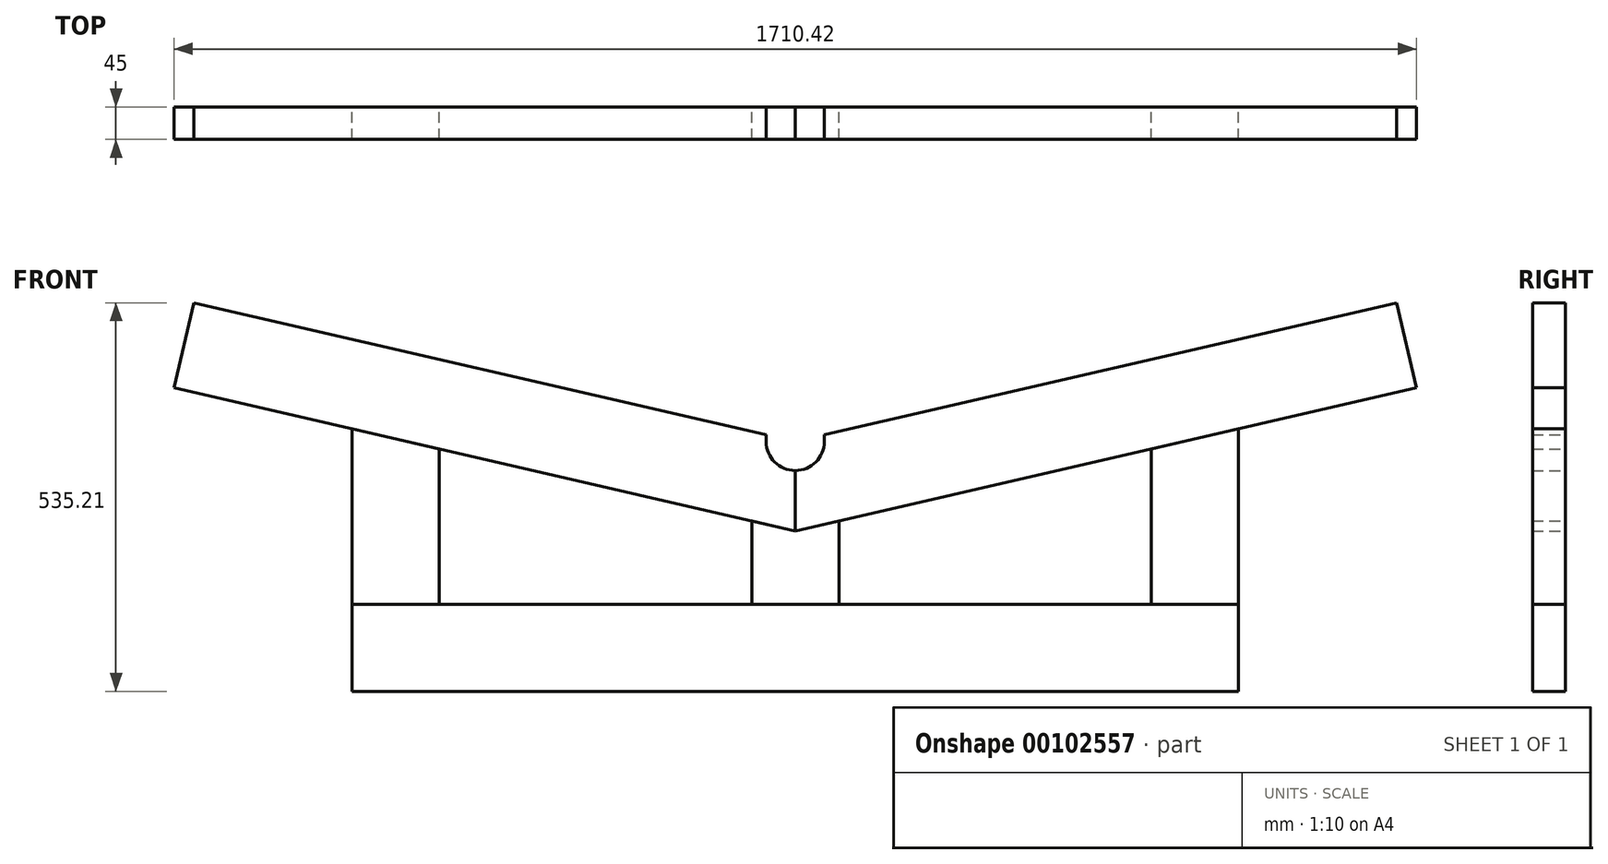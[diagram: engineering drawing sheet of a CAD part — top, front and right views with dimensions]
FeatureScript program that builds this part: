
annotation { "Feature Type Name" : "Feature", "Feature Type Description" : "" }
export const myFeature = defineFeature(function(context is Context, id is Id, definition is map)
    precondition{}
    {
        {
            var Q0;
            Q0=qCreatedBy(makeId("Front.planeOp"),FACE);
            var sketch = newSketch(context, id + "F0", { "sketchPlane" : qUnion([Q0])});
            skLineSegment(sketch, "E0.bottom", {"start": v(0, 0) * mm, "end": v(1220, 0) * mm});
            skLineSegment(sketch, "E0.top", {"start": v(0, 120) * mm, "end": v(1220, 120) * mm});
            skLineSegment(sketch, "E0.left", {"start": v(0, 0) * mm, "end": v(0, 120) * mm});
            skLineSegment(sketch, "E0.right", {"start": v(1220, 0) * mm, "end": v(1220, 120) * mm});
            skSolve(sketch);
        }
        {
            var Q0;
            Q0 = qSketchRegion(id + "F0", true);
            extrude(context, id + "F1", {"entities" : qUnion([Q0]), "depth" : 45 * mm});
        }
        {
            var Q0;
            Q0=qCreatedBy(makeId("Front.planeOp"),FACE);
            var sketch = newSketch(context, id + "F2", { "sketchPlane" : qUnion([Q0])});
            skLineSegment(sketch, "E1", {"start": v(610, 0) * mm, "end": v(610, 344) * mm, "construction": true});
            skLineSegment(sketch, "E2", {"start": v(570, 353.23) * mm, "end": v(-218.21, 535.2) * mm});
            skLineSegment(sketch, "E3.0", {"start": v(610, 220.84) * mm, "end": v(-245.2, 418.28) * mm});
            skLineSegment(sketch, "E4", {"start": v(-218.21, 535.2) * mm, "end": v(-245.2, 418.28) * mm});
            skLineSegment(sketch, "E5", {"start": v(610, 220.84) * mm, "end": v(610, 304) * mm});
            skArc(sketch, "E6", {"start": v(570, 344) * mm, "mid": v(581.72, 315.72) * mm, "end": v(610, 304) * mm});
            skLineSegment(sketch, "E7", {"start": v(570, 344) * mm, "end": v(570, 353.23) * mm});
            skSolve(sketch);
        }
        {
            var Q0;
            Q0 = qSketchRegion(id + "F2", true);
            extrude(context, id + "F3", {"entities" : qUnion([Q0]), "depth" : 45 * mm});
        }
        {
            var Q0;
            Q0=qCreatedBy(makeId("Front.planeOp"),FACE);
            var sketch = newSketch(context, id + "F4", { "sketchPlane" : qUnion([Q0])});
            skLineSegment(sketch, "E8", {"start": v(0, 120) * mm, "end": v(0, 361.67) * mm});
            skLineSegment(sketch, "E9.0", {"start": v(120, 120) * mm, "end": v(120, 333.97) * mm});
            skLineSegment(sketch, "E10", {"start": v(0, 361.67) * mm, "end": v(120, 333.97) * mm});
            skLineSegment(sketch, "E11", {"start": v(0, 120) * mm, "end": v(120, 120) * mm});
            skSolve(sketch);
        }
        {
            var Q0;
            Q0 = qSketchRegion(id + "F4", true);
            extrude(context, id + "F5", {"entities" : qUnion([Q0]), "depth" : 45 * mm});
        }
        {
            var Q0;
            Q0=qCreatedBy(makeId("Right.planeOp"),FACE);
            cPlane(context, id + "F6", {"entities" : qUnion([Q0]), "cplaneType" : CPlaneType.OFFSET, "offset" : 610 * mm, "width" : 150 * mm, "height" : 150 * mm});
        }
        {
            var Q0;
            Q0=makeQuery(id+"F1.opExtrude","SWEPT_BODY",BODY,{"disambiguationData":[OSD([sQuery(id+"F0.wireOp",EDGE,"E0.bottom"),sQuery(id+"F0.wireOp",EDGE,"E0.top"),sQuery(id+"F0.wireOp",EDGE,"E0.left"),sQuery(id+"F0.wireOp",EDGE,"E0.right")])]});
            var Q1;
            Q1=makeQuery(id+"F3.opExtrude","SWEPT_BODY",BODY,{"disambiguationData":[OSD([sQuery(id+"F2.wireOp",EDGE,"E2"),sQuery(id+"F2.wireOp",EDGE,"E3.0"),sQuery(id+"F2.wireOp",EDGE,"E4"),sQuery(id+"F2.wireOp",EDGE,"E5"),sQuery(id+"F2.wireOp",EDGE,"E6"),sQuery(id+"F2.wireOp",EDGE,"E7")])]});
            var Q2;
            Q2=makeQuery(id+"F5.opExtrude","SWEPT_BODY",BODY,{"disambiguationData":[OSD([sQuery(id+"F4.wireOp",EDGE,"E8"),sQuery(id+"F4.wireOp",EDGE,"E9.0"),sQuery(id+"F4.wireOp",EDGE,"E10"),sQuery(id+"F4.wireOp",EDGE,"E11")])]});
            var Q3;
            Q3=qCreatedBy(id+"F6.planeOp",FACE);
            mirror(context, id + "F7", {"entities" : qUnion([Q0, Q1, Q2]), "mirrorPlane" : qUnion([Q3])});
        }
        {
            var Q0;
            Q0=qCreatedBy(makeId("Front.planeOp"),FACE);
            var sketch = newSketch(context, id + "F8", { "sketchPlane" : qUnion([Q0])});
            skLineSegment(sketch, "E12", {"start": v(610, 120) * mm, "end": v(610, 220.84) * mm, "construction": true});
            skLineSegment(sketch, "E13.0", {"start": v(670, 120) * mm, "end": v(670, 234.7) * mm});
            skLineSegment(sketch, "E14.MirrorCS", {"start": v(550, 120) * mm, "end": v(550, 234.7) * mm});
            skLineSegment(sketch, "E15", {"start": v(550, 234.7) * mm, "end": v(610, 220.84) * mm});
            skLineSegment(sketch, "E16", {"start": v(610, 220.84) * mm, "end": v(670, 234.7) * mm});
            skLineSegment(sketch, "E17", {"start": v(670, 120) * mm, "end": v(550, 120) * mm});
            skSolve(sketch);
        }
        {
            var Q0;
            Q0 = qSketchRegion(id + "F8", true);
            extrude(context, id + "F9", {"entities" : qUnion([Q0]), "depth" : 45 * mm});
        }
        {
            var Q0;
            Q0=makeQuery(id+"F7.opPattern","COPY",BODY,{"derivedFrom":makeQuery(id+"F1.opExtrude","SWEPT_BODY",BODY,{"disambiguationData":[OSD([sQuery(id+"F0.wireOp",EDGE,"E0.bottom"),sQuery(id+"F0.wireOp",EDGE,"E0.top"),sQuery(id+"F0.wireOp",EDGE,"E0.left"),sQuery(id+"F0.wireOp",EDGE,"E0.right")])]}),"instanceName":"1"});
            deleteBodies(context, id + "F10", {"entities" : qUnion([Q0])});
        }
    });
